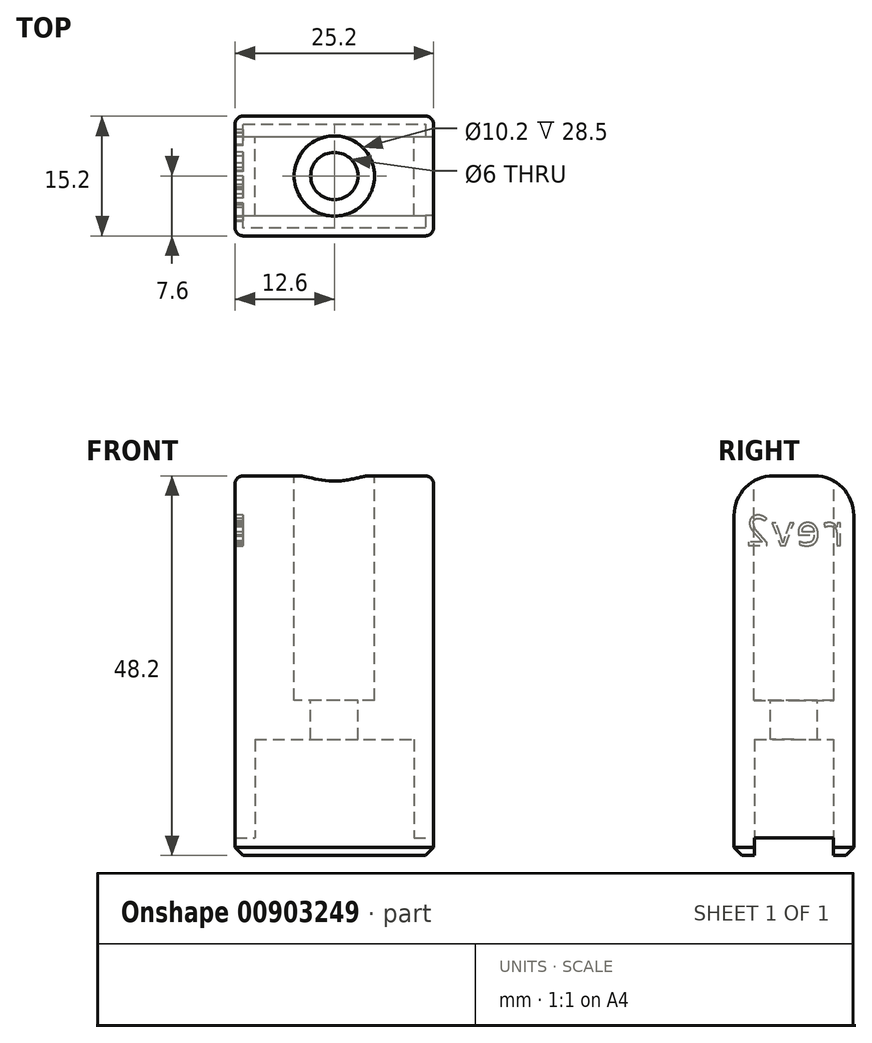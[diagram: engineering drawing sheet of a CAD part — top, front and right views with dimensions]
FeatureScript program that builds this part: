
annotation { "Feature Type Name" : "Feature", "Feature Type Description" : "" }
export const myFeature = defineFeature(function(context is Context, id is Id, definition is map)
    precondition{}
    {
        {
            var Q0;
            Q0=qCreatedBy(makeId("Top.planeOp"),FACE);
            var sketch = newSketch(context, id + "F0", { "sketchPlane" : qUnion([Q0])});
            skLineSegment(sketch, "E0.top", {"start": v(-12.6, -7.6) * mm, "end": v(12.6, -7.6) * mm});
            skLineSegment(sketch, "E0.left", {"start": v(-12.6, 7.6) * mm, "end": v(-12.6, -7.6) * mm});
            skLineSegment(sketch, "E0.right", {"start": v(12.6, 7.6) * mm, "end": v(12.6, -7.6) * mm});
            skLineSegment(sketch, "E1", {"start": v(-12.6, 7.6) * mm, "end": v(12.6, 7.6) * mm});
            skSolve(sketch);
        }
        {
            var Q0;
            Q0=makeQuery(id+"F0.imprint","IMPRINT",FACE,{"disambiguationData":[TD([[makeQuery(id+"F0.imprint","IMPRINT",EDGE,{"derivedFrom":sQuery(id+"F0.wireOp",EDGE,"E0.top")}),1.0]])]});
            extrude(context, id + "F1", {"entities" : qUnion([Q0]), "oppositeDirection" : true, "depth" : 46 * mm, "offsetDistance" : 25 * mm});
        }
        {
            var Q0;
            Q0=makeQuery(id+"F1.opExtrude","CAP_FACE",FACE,{"disambiguationData":[OSD([sQuery(id+"F0.wireOp",EDGE,"E0.top"),sQuery(id+"F0.wireOp",EDGE,"E0.left"),sQuery(id+"F0.wireOp",EDGE,"E0.right"),sQuery(id+"F0.wireOp",EDGE,"E1")])],"isStart":false});
            var sketch = newSketch(context, id + "F2", { "sketchPlane" : qUnion([Q0])});
            skLineSegment(sketch, "E2.top", {"start": v(-10.1, -5) * mm, "end": v(10.1, -5) * mm});
            skLineSegment(sketch, "E2.left", {"start": v(-10.1, 5) * mm, "end": v(-10.1, -5) * mm});
            skLineSegment(sketch, "E2.right", {"start": v(10.1, 5) * mm, "end": v(10.1, -5) * mm});
            skLineSegment(sketch, "E3", {"start": v(-10.1, 5) * mm, "end": v(10.1, 5) * mm});
            skSolve(sketch);
        }
        {
            var Q0;
            Q0=makeQuery(id+"F2.imprint","IMPRINT",FACE,{"disambiguationData":[TD([[makeQuery(id+"F2.imprint","IMPRINT",EDGE,{"derivedFrom":sQuery(id+"F2.wireOp",EDGE,"E2.top")}),1.0]])]});
            extrude(context, id + "F3", {"entities" : qUnion([Q0]), "operationType" : NewBodyOperationType.REMOVE, "oppositeDirection" : true, "depth" : 12.5 * mm, "offsetDistance" : 25 * mm});
        }
        {
            var Q0;
            Q0=makeQuery(id+"F1.opExtrude","CAP_FACE",FACE,{"disambiguationData":[OSD([sQuery(id+"F0.wireOp",EDGE,"E0.top"),sQuery(id+"F0.wireOp",EDGE,"E0.left"),sQuery(id+"F0.wireOp",EDGE,"E0.right"),sQuery(id+"F0.wireOp",EDGE,"E1")])],"isStart":true});
            var sketch = newSketch(context, id + "F4", { "sketchPlane" : qUnion([Q0])});
            skCircle(sketch, "E4", {"center": v(0, 0) * mm, "radius": 5.1 * mm});
            skSolve(sketch);
        }
        {
            var Q0;
            Q0=makeQuery(id+"F4.imprint","IMPRINT",FACE,{"disambiguationData":[TD([[makeQuery(id+"F4.imprint","IMPRINT",EDGE,{"derivedFrom":sQuery(id+"F4.wireOp",EDGE,"E4")}),1.0]])]});
            extrude(context, id + "F5", {"entities" : qUnion([Q0]), "operationType" : NewBodyOperationType.REMOVE, "oppositeDirection" : true, "depth" : 28.5 * mm, "offsetDistance" : 25 * mm});
        }
        {
            var Q0;
            Q0=makeQuery(id+"F5.boolean.opBoolean","COPY",FACE,{"derivedFrom":makeQuery(id+"F5.opExtrude","CAP_FACE",FACE,{"disambiguationData":[OSD([sQuery(id+"F4.wireOp",EDGE,"E4")])],"isStart":false})});
            var sketch = newSketch(context, id + "F6", { "sketchPlane" : qUnion([Q0])});
            skCircle(sketch, "E5", {"center": v(0, 0) * mm, "radius": 3 * mm});
            skSolve(sketch);
        }
        {
            var Q0;
            Q0=makeQuery(id+"F6.imprint","IMPRINT",FACE,{"disambiguationData":[TD([[makeQuery(id+"F6.imprint","IMPRINT",EDGE,{"derivedFrom":sQuery(id+"F6.wireOp",EDGE,"E5")}),1.0]])]});
            extrude(context, id + "F7", {"entities" : qUnion([Q0]), "operationType" : NewBodyOperationType.REMOVE, "oppositeDirection" : true, "depth" : 25 * mm, "offsetDistance" : 25 * mm});
        }
        {
            var Q0;
            Q0=makeQuery(id+"F1.opExtrude","CAP_FACE",FACE,{"disambiguationData":[OSD([sQuery(id+"F0.wireOp",EDGE,"E0.top"),sQuery(id+"F0.wireOp",EDGE,"E0.left"),sQuery(id+"F0.wireOp",EDGE,"E0.right"),sQuery(id+"F0.wireOp",EDGE,"E1")])],"isStart":false});
            var sketch = newSketch(context, id + "F8", { "sketchPlane" : qUnion([Q0])});
            skLineSegment(sketch, "E6.bottom", {"start": v(-12.6, 7.6) * mm, "end": v(12.6, 7.6) * mm});
            skLineSegment(sketch, "E6.top", {"start": v(-12.6, 5) * mm, "end": v(12.6, 5) * mm});
            skLineSegment(sketch, "E6.left", {"start": v(-12.6, 7.6) * mm, "end": v(-12.6, 5) * mm});
            skLineSegment(sketch, "E6.right", {"start": v(12.6, 7.6) * mm, "end": v(12.6, 5) * mm});
            skPoint(sketch, "E7.oppositeSnap0", {"position": v(12.6, 0) * mm});
            skLineSegment(sketch, "E7.bottom", {"start": v(-12.6, -7.6) * mm, "end": v(12.6, -7.6) * mm});
            skLineSegment(sketch, "E7.top", {"start": v(-12.6, -5) * mm, "end": v(12.6, -5) * mm});
            skLineSegment(sketch, "E7.left", {"start": v(-12.6, -7.6) * mm, "end": v(-12.6, -5) * mm});
            skLineSegment(sketch, "E7.right", {"start": v(12.6, -7.6) * mm, "end": v(12.6, -5) * mm});
            skSolve(sketch);
        }
        {
            var Q0;
            Q0=makeQuery(id+"F8.imprint","IMPRINT",FACE,{"disambiguationData":[TD([[makeQuery(id+"F8.imprint","IMPRINT",EDGE,{"derivedFrom":sQuery(id+"F8.wireOp",EDGE,"E6.bottom")}),-1.0]])]});
            var Q1;
            Q1=makeQuery(id+"F8.imprint","IMPRINT",FACE,{"disambiguationData":[TD([[makeQuery(id+"F8.imprint","IMPRINT",EDGE,{"derivedFrom":sQuery(id+"F8.wireOp",EDGE,"E7.bottom")}),1.0]])]});
            extrude(context, id + "F9", {"entities" : qUnion([Q0, Q1]), "operationType" : NewBodyOperationType.ADD, "depth" : 2.2 * mm, "offsetDistance" : 25 * mm});
        }
        {
            var Q0;
            Q0=makeQuery(id+"F1.opExtrude","CAP_EDGE",EDGE,{"disambiguationData":[OSD([sQuery(id+"F0.wireOp",EDGE,"E0.top")])],"isStart":true});
            var Q1;
            Q1=makeQuery(id+"F1.opExtrude","CAP_EDGE",EDGE,{"disambiguationData":[OSD([sQuery(id+"F0.wireOp",EDGE,"E1")])],"isStart":true});
            fillet(context, id + "F10", {"entities" : qUnion([Q0, Q1]), "radius" : 5 * mm, "tangentPropagation" : true, "allowEdgeOverflow" : false});
        }
        {
            var Q0;
            Q0=makeQuery(id+"F9.boolean.opBoolean","MERGE",EDGE,{"derivedFrom":[makeQuery(id+"F1.opExtrude","SWEPT_EDGE",EDGE,{"disambiguationData":[OSD([sQuery(id+"F0.wireOp",EDGE,"E0.top"),sQuery(id+"F0.wireOp",EDGE,"E0.left")])]}),makeQuery(id+"F9.opExtrude","SWEPT_EDGE",EDGE,{"disambiguationData":[OSD([sQuery(id+"F8.wireOp",EDGE,"E6.bottom"),sQuery(id+"F8.wireOp",EDGE,"E6.left")])]})]});
            var Q1;
            Q1=makeQuery(id+"F9.boolean.opBoolean","MERGE",EDGE,{"derivedFrom":[makeQuery(id+"F1.opExtrude","SWEPT_EDGE",EDGE,{"disambiguationData":[OSD([sQuery(id+"F0.wireOp",EDGE,"E0.left"),sQuery(id+"F0.wireOp",EDGE,"E1")])]}),makeQuery(id+"F9.opExtrude","SWEPT_EDGE",EDGE,{"disambiguationData":[OSD([sQuery(id+"F8.wireOp",EDGE,"E7.bottom"),sQuery(id+"F8.wireOp",EDGE,"E7.left")])]})]});
            var Q2;
            Q2=makeQuery(id+"F9.boolean.opBoolean","MERGE",EDGE,{"derivedFrom":[makeQuery(id+"F1.opExtrude","SWEPT_EDGE",EDGE,{"disambiguationData":[OSD([sQuery(id+"F0.wireOp",EDGE,"E0.top"),sQuery(id+"F0.wireOp",EDGE,"E0.right")])]}),makeQuery(id+"F9.opExtrude","SWEPT_EDGE",EDGE,{"disambiguationData":[OSD([sQuery(id+"F8.wireOp",EDGE,"E6.bottom"),sQuery(id+"F8.wireOp",EDGE,"E6.right")])]})]});
            var Q3;
            Q3=makeQuery(id+"F9.boolean.opBoolean","MERGE",EDGE,{"derivedFrom":[makeQuery(id+"F1.opExtrude","SWEPT_EDGE",EDGE,{"disambiguationData":[OSD([sQuery(id+"F0.wireOp",EDGE,"E0.right"),sQuery(id+"F0.wireOp",EDGE,"E1")])]}),makeQuery(id+"F9.opExtrude","SWEPT_EDGE",EDGE,{"disambiguationData":[OSD([sQuery(id+"F8.wireOp",EDGE,"E7.bottom"),sQuery(id+"F8.wireOp",EDGE,"E7.right")])]})]});
            fillet(context, id + "F11", {"entities" : qUnion([Q0, Q1, Q2, Q3]), "radius" : 1 * mm, "tangentPropagation" : true, "allowEdgeOverflow" : false});
        }
        {
            var Q0;
            Q0=makeQuery(id+"F9.opExtrude","CAP_EDGE",EDGE,{"disambiguationData":[OSD([sQuery(id+"F8.wireOp",EDGE,"E6.bottom")])],"isStart":false});
            var Q1;
            Q1=makeQuery(id+"F9.opExtrude","CAP_EDGE",EDGE,{"disambiguationData":[OSD([sQuery(id+"F8.wireOp",EDGE,"E7.bottom")])],"isStart":false});
            chamfer(context, id + "F12", {"entities" : qUnion([Q0, Q1]), "width" : 1 * mm, "tangentPropagation" : true});
        }
        {
            var Q0;
            Q0=makeQuery(id+"F9.boolean.opBoolean","MERGE",FACE,{"derivedFrom":[makeQuery(id+"F1.opExtrude","SWEPT_FACE",FACE,{"disambiguationData":[OSD([sQuery(id+"F0.wireOp",EDGE,"E0.left")])]}),makeQuery(id+"F9.opExtrude","SWEPT_FACE",FACE,{"disambiguationData":[OSD([sQuery(id+"F8.wireOp",EDGE,"E6.left")])]}),makeQuery(id+"F9.opExtrude","SWEPT_FACE",FACE,{"disambiguationData":[OSD([sQuery(id+"F8.wireOp",EDGE,"E7.left")])]})]});
            var sketch = newSketch(context, id + "F13", { "sketchPlane" : qUnion([Q0])});
            skText(sketch, "E8", { "text": "rev2", "fontName": "DroidSansMono.ttf"});
            const initialGuessF13  = {"E8": [-0.0066, -0.00884, 1, 0, 0.00384]};
            skSetInitialGuess(sketch, initialGuessF13);
            skSolve(sketch);
        }
        {
            var Q0;
            Q0 = qSketchRegion(id + "F13", true);
            extrude(context, id + "F14", {"entities" : qUnion([Q0]), "operationType" : NewBodyOperationType.REMOVE, "oppositeDirection" : true, "depth" : 1 * mm, "offsetDistance" : 25 * mm});
        }
    });
